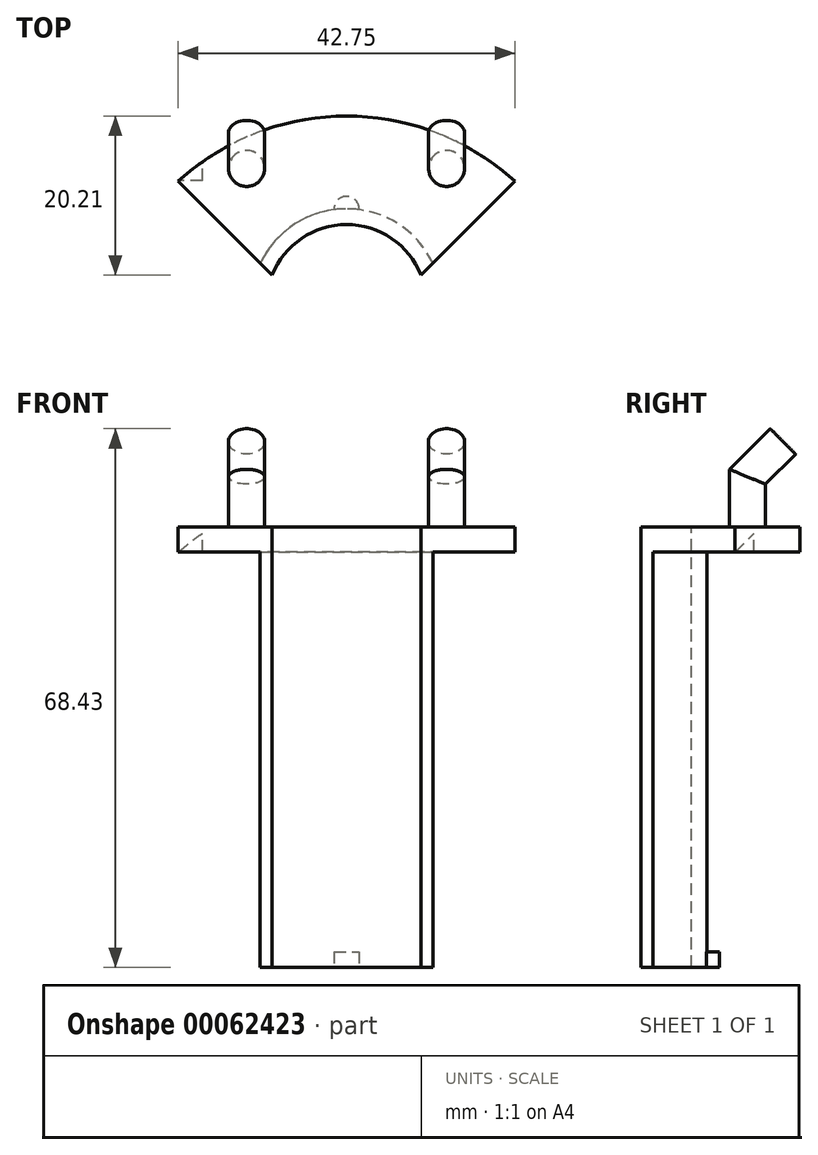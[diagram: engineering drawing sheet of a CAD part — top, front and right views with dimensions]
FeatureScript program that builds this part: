
annotation { "Feature Type Name" : "Feature", "Feature Type Description" : "" }
export const myFeature = defineFeature(function(context is Context, id is Id, definition is map)
    precondition{}
    {
        {
            var Q0;
            Q0=qCreatedBy(makeId("Top.planeOp"),FACE);
            var sketch = newSketch(context, id + "F0", { "sketchPlane" : qUnion([Q0])});
            skLineSegment(sketch, "E0.bottom", {"start": v(0, 0) * mm, "end": v(31.75, 0) * mm});
            skLineSegment(sketch, "E0.top", {"start": v(0, 9.52) * mm, "end": v(31.75, 9.52) * mm});
            skLineSegment(sketch, "E0.left", {"start": v(0, 0) * mm, "end": v(0, 9.52) * mm});
            skLineSegment(sketch, "E0.right", {"start": v(31.75, 0) * mm, "end": v(31.75, 9.52) * mm});
            skSolve(sketch);
        }
        {
            var Q0;
            Q0=makeQuery(id+"F0.imprint","IMPRINT",FACE,{"disambiguationData":[TD([[makeQuery(id+"F0.imprint","IMPRINT",EDGE,{"derivedFrom":sQuery(id+"F0.wireOp",EDGE,"E0.bottom")}),1.0]])]});
            extrude(context, id + "F1", {"entities" : qUnion([Q0]), "depth" : 3.17 * mm});
        }
        {
            var Q0;
            Q0=makeQuery(id+"F1.opExtrude","SWEPT_FACE",FACE,{"disambiguationData":[OSD([sQuery(id+"F0.wireOp",EDGE,"E0.right")])]});
            cPlane(context, id + "F2", {"entities" : qUnion([Q0]), "cplaneType" : CPlaneType.OFFSET, "offset" : 3.17 * mm, "oppositeDirection" : true, "width" : 152.4 * mm, "height" : 152.4 * mm});
        }
        {
            var Q0;
            Q0=qCreatedBy(id+"F2.planeOp",FACE);
            var sketch = newSketch(context, id + "F3", { "sketchPlane" : qUnion([Q0])});
            skLineSegment(sketch, "E1", {"start": v(7.14, 3.18) * mm, "end": v(7.14, 9.53) * mm});
            skLineSegment(sketch, "E2", {"start": v(7.14, 9.53) * mm, "end": v(11.63, 14.02) * mm});
            skSolve(sketch);
        }
        {
            var Q0;
            Q0=makeQuery(id+"F1.opExtrude","CAP_FACE",FACE,{"disambiguationData":[OSD([sQuery(id+"F0.wireOp",EDGE,"E0.bottom"),sQuery(id+"F0.wireOp",EDGE,"E0.top"),sQuery(id+"F0.wireOp",EDGE,"E0.left"),sQuery(id+"F0.wireOp",EDGE,"E0.right")])],"isStart":false});
            var sketch = newSketch(context, id + "F4", { "sketchPlane" : qUnion([Q0])});
            skCircle(sketch, "E3", {"center": v(28.57, 7.14) * mm, "radius": 2.29 * mm});
            skSolve(sketch);
        }
        {
            var Q0;
            Q0=makeQuery(id+"F4.imprint","IMPRINT",FACE,{"disambiguationData":[TD([[makeQuery(id+"F4.imprint","IMPRINT",EDGE,{"derivedFrom":sQuery(id+"F4.wireOp",EDGE,"E3")}),1.0]])]});
            var Q1;
            Q1=sQuery(id+"F3.wireOp",EDGE,"E1");
            var Q2;
            Q2=sQuery(id+"F3.wireOp",EDGE,"E2");
            sweep(context, id + "F5", {"operationType" : NewBodyOperationType.ADD, "profiles" : qUnion([Q0]), "path" : qUnion([Q1, Q2])});
        }
        {
            var Q0;
            Q0=qCreatedBy(id+"F2.planeOp",FACE);
            cPlane(context, id + "F6", {"entities" : qUnion([Q0]), "cplaneType" : CPlaneType.OFFSET, "offset" : 25.4 * mm, "oppositeDirection" : true, "width" : 152.4 * mm, "height" : 152.4 * mm});
        }
        {
            var Q0;
            Q0=qCreatedBy(id+"F6.planeOp",FACE);
            var sketch = newSketch(context, id + "F7", { "sketchPlane" : qUnion([Q0])});
            skLineSegment(sketch, "E4.0", {"start": v(7.14, 3.18) * mm, "end": v(7.14, 9.53) * mm});
            skLineSegment(sketch, "E4.1", {"start": v(7.14, 9.53) * mm, "end": v(11.63, 14.02) * mm});
            skSolve(sketch);
        }
        {
            var Q0;
            Q0=makeQuery(id+"F1.opExtrude","CAP_FACE",FACE,{"disambiguationData":[OSD([sQuery(id+"F0.wireOp",EDGE,"E0.bottom"),sQuery(id+"F0.wireOp",EDGE,"E0.top"),sQuery(id+"F0.wireOp",EDGE,"E0.left"),sQuery(id+"F0.wireOp",EDGE,"E0.right")])],"isStart":false});
            var sketch = newSketch(context, id + "F8", { "sketchPlane" : qUnion([Q0])});
            skCircle(sketch, "E5", {"center": v(3.17, 7.14) * mm, "radius": 2.29 * mm});
            skSolve(sketch);
        }
        {
            var Q0;
            Q0=makeQuery(id+"F8.imprint","IMPRINT",FACE,{"disambiguationData":[TD([[makeQuery(id+"F8.imprint","IMPRINT",EDGE,{"derivedFrom":sQuery(id+"F8.wireOp",EDGE,"E5")}),1.0]])]});
            var Q1;
            Q1=sQuery(id+"F7.wireOp",EDGE,"E4.0");
            var Q2;
            Q2=sQuery(id+"F7.wireOp",EDGE,"E4.1");
            sweep(context, id + "F9", {"operationType" : NewBodyOperationType.ADD, "profiles" : qUnion([Q0]), "path" : qUnion([Q1, Q2])});
        }
        {
            var Q0;
            Q0=makeQuery(id+"F1.opExtrude","CAP_FACE",FACE,{"disambiguationData":[OSD([sQuery(id+"F0.wireOp",EDGE,"E0.bottom"),sQuery(id+"F0.wireOp",EDGE,"E0.top"),sQuery(id+"F0.wireOp",EDGE,"E0.left"),sQuery(id+"F0.wireOp",EDGE,"E0.right")])],"isStart":false});
            var sketch = newSketch(context, id + "F10", { "sketchPlane" : qUnion([Q0])});
            skArc(sketch, "E6", {"start": v(37.25, 5.5) * mm, "mid": v(15.88, 13.78) * mm, "end": v(-5.5, 5.5) * mm});
            skArc(sketch, "E7", {"start": v(25.32, -6.43) * mm, "mid": v(15.88, 0) * mm, "end": v(6.43, -6.43) * mm});
            skLineSegment(sketch, "E8", {"start": v(-5.5, 5.5) * mm, "end": v(6.43, -6.43) * mm});
            skLineSegment(sketch, "E9", {"start": v(25.32, -6.43) * mm, "end": v(37.25, 5.5) * mm});
            skSolve(sketch);
        }
        {
            var Q0;
            Q0=qSketchRegion(id+"F10",true);
            var Q1;
            Q1=makeQuery(id+"F1.opExtrude","CAP_FACE",FACE,{"disambiguationData":[OSD([sQuery(id+"F0.wireOp",EDGE,"E0.bottom"),sQuery(id+"F0.wireOp",EDGE,"E0.top"),sQuery(id+"F0.wireOp",EDGE,"E0.left"),sQuery(id+"F0.wireOp",EDGE,"E0.right")])],"isStart":true});
            extrude(context, id + "F11", {"entities" : qUnion([Q0]), "operationType" : NewBodyOperationType.ADD, "endBound" : BoundingType.UP_TO_SURFACE, "oppositeDirection" : true, "endBoundEntityFace" : qUnion([Q1]), "depth" : 25.4 * mm});
        }
        {
            var Q0;
            {var subQ0=sQuery(id+"F0.wireOp",EDGE,"E0.right");var subQ1=sQuery(id+"F0.wireOp",EDGE,"E0.left");var subQ2=sQuery(id+"F0.wireOp",EDGE,"E0.top");var subQ3=sQuery(id+"F0.wireOp",EDGE,"E0.bottom");Q0=makeQuery(id+"F11.boolean.opBoolean","MERGE",FACE,{"derivedFrom":[makeQuery(id+"F1.opExtrude","CAP_FACE",FACE,{"disambiguationData":[OSD([subQ3,subQ2,subQ1,subQ0])],"isStart":true}),makeQuery(id+"F11.opExtrude","CAP_FACE",FACE,{"disambiguationData":[OSD([subQ3,subQ2,subQ1,subQ0])],"isStart":false})]});}
            var sketch = newSketch(context, id + "F12", { "sketchPlane" : qUnion([Q0])});
            skArc(sketch, "E10.0", {"start": v(4.9, 4.9) * mm, "mid": v(15.88, -2) * mm, "end": v(26.84, 4.9) * mm});
            skArc(sketch, "E11.0", {"start": v(6.43, 6.43) * mm, "mid": v(15.88, 0) * mm, "end": v(25.32, 6.43) * mm});
            skLineSegment(sketch, "E12", {"start": v(4.9, 4.9) * mm, "end": v(6.43, 6.43) * mm});
            skLineSegment(sketch, "E13", {"start": v(26.84, 4.9) * mm, "end": v(25.32, 6.43) * mm});
            skSolve(sketch);
        }
        {
            var Q0;
            Q0=qSketchRegion(id+"F12",true);
            extrude(context, id + "F13", {"entities" : qUnion([Q0]), "operationType" : NewBodyOperationType.ADD, "depth" : 52.8 * mm});
        }
        {
            var Q0;
            Q0=makeQuery(id+"F9.opSweep","CAP_FACE",FACE,{"disambiguationData":[OSD([sQuery(id+"F7.wireOp",VERTEX,"E4.1.end"),sQuery(id+"F8.wireOp",EDGE,"E5")])],"isStart":false});
            var sketch = newSketch(context, id + "F14", { "sketchPlane" : qUnion([Q0])});
            skLineSegment(sketch, "E14.bottom", {"start": v(2.45, -3.97) * mm, "end": v(29.3, -3.97) * mm});
            skLineSegment(sketch, "E14.top", {"start": v(2.45, -10.25) * mm, "end": v(29.3, -10.25) * mm});
            skLineSegment(sketch, "E14.left", {"start": v(2.45, -3.97) * mm, "end": v(2.45, -10.25) * mm});
            skLineSegment(sketch, "E14.right", {"start": v(29.3, -3.97) * mm, "end": v(29.3, -10.25) * mm});
            skSolve(sketch);
        }
        {
            var Q0;
            Q0=makeQuery(id+"F14.imprint","IMPRINT",FACE,{"disambiguationData":[TD([[makeQuery(id+"F14.imprint","IMPRINT",EDGE,{"derivedFrom":sQuery(id+"F14.wireOp",EDGE,"E14.top")}),1.0]])]});
            extrude(context, id + "F15", {"entities" : qUnion([Q0]), "operationType" : NewBodyOperationType.REMOVE, "oppositeDirection" : true, "depth" : 25.4 * mm});
        }
        {
            var Q0;
            Q0=makeQuery(id+"F13.opExtrude","CAP_FACE",FACE,{"disambiguationData":[OSD([sQuery(id+"F12.wireOp",EDGE,"E10.0"),sQuery(id+"F12.wireOp",EDGE,"E11.0"),sQuery(id+"F12.wireOp",EDGE,"E12"),sQuery(id+"F12.wireOp",EDGE,"E13")])],"isStart":false});
            var sketch = newSketch(context, id + "F16", { "sketchPlane" : qUnion([Q0])});
            skArc(sketch, "E15", {"start": v(14.3, -1.9) * mm, "mid": v(15.88, -3.59) * mm, "end": v(17.46, -1.9) * mm});
            skArc(sketch, "E16", {"start": v(14.3, -1.9) * mm, "mid": v(15.88, -2) * mm, "end": v(17.46, -1.9) * mm});
            skSolve(sketch);
        }
        {
            var Q0;
            Q0=makeQuery(id+"F16.imprint","IMPRINT",FACE,{"disambiguationData":[TD([[makeQuery(id+"F16.imprint","IMPRINT",EDGE,{"derivedFrom":sQuery(id+"F16.wireOp",EDGE,"E15")}),1.0]])]});
            extrude(context, id + "F17", {"entities" : qUnion([Q0]), "operationType" : NewBodyOperationType.ADD, "oppositeDirection" : true, "depth" : 2 * mm});
        }
    });
